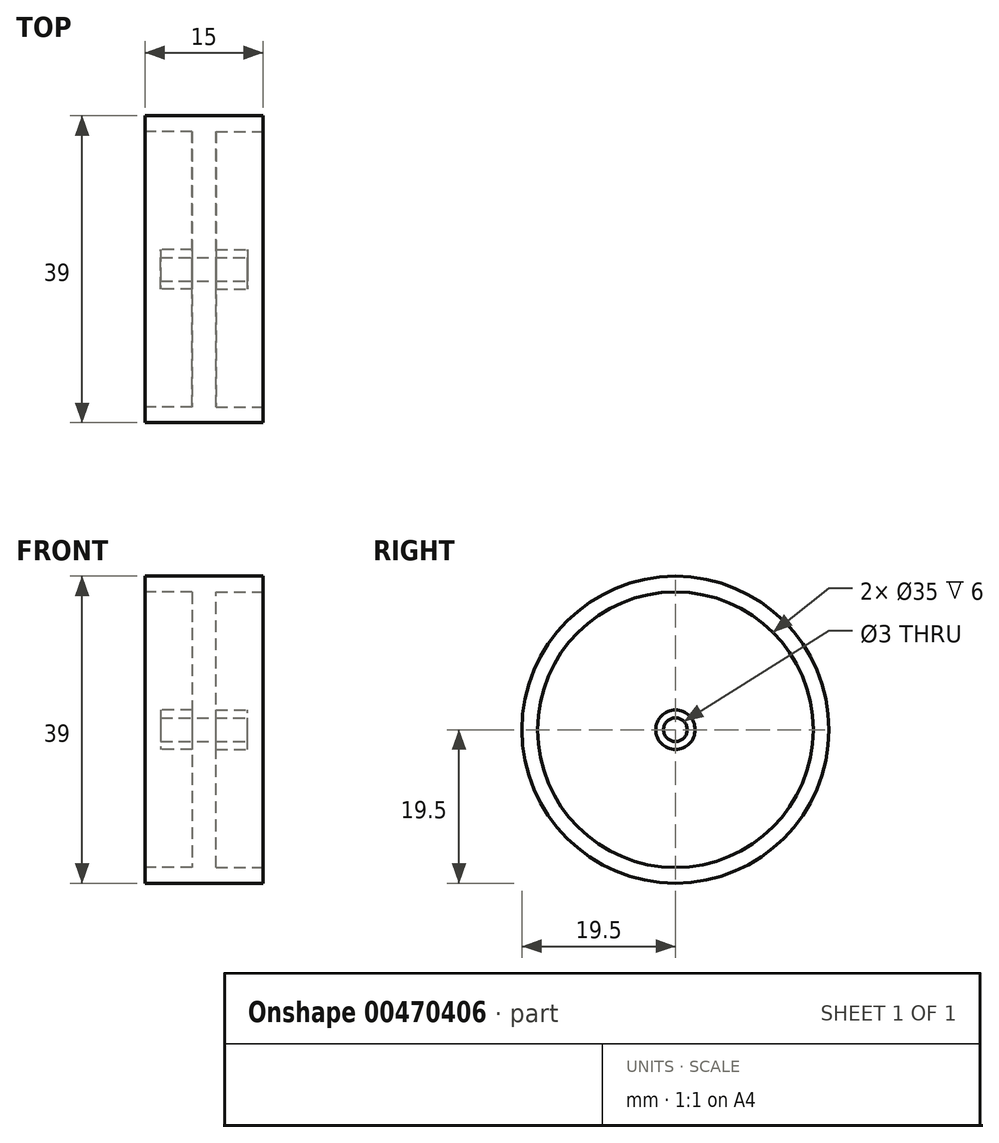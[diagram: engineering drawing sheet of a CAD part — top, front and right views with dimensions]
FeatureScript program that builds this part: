
annotation { "Feature Type Name" : "Feature", "Feature Type Description" : "" }
export const myFeature = defineFeature(function(context is Context, id is Id, definition is map)
    precondition{}
    {
        {
            var Q0;
            Q0=qCreatedBy(makeId("Right.planeOp"),FACE);
            var sketch = newSketch(context, id + "F0", { "sketchPlane" : qUnion([Q0])});
            skCircle(sketch, "E0", {"center": v(0, 0) * mm, "radius": 19.5 * mm});
            skSolve(sketch);
        }
        {
            var Q0;
            Q0=makeQuery(id+"F0.imprint","IMPRINT",FACE,{"disambiguationData":[TD([[makeQuery(id+"F0.imprint","IMPRINT",EDGE,{"derivedFrom":sQuery(id+"F0.wireOp",EDGE,"E0")}),1.0]])]});
            extrude(context, id + "F1", {"entities" : qUnion([Q0]), "endBound" : BoundingType.SYMMETRIC, "depth" : 15 * mm});
        }
        {
            var Q0;
            Q0=makeQuery(id+"F1.opExtrude","CAP_FACE",FACE,{"disambiguationData":[OSD([sQuery(id+"F0.wireOp",EDGE,"E0")])],"isStart":false});
            var sketch = newSketch(context, id + "F2", { "sketchPlane" : qUnion([Q0])});
            skCircle(sketch, "E1", {"center": v(0, 0) * mm, "radius": 17.5 * mm});
            skSolve(sketch);
        }
        {
            var Q0;
            Q0=makeQuery(id+"F1.opExtrude","CAP_FACE",FACE,{"disambiguationData":[OSD([sQuery(id+"F0.wireOp",EDGE,"E0")])],"isStart":true});
            var sketch = newSketch(context, id + "F3", { "sketchPlane" : qUnion([Q0])});
            skCircle(sketch, "E2", {"center": v(0, 0) * mm, "radius": 17.5 * mm});
            skSolve(sketch);
        }
        {
            var Q0;
            Q0=makeQuery(id+"F3.imprint","IMPRINT",FACE,{"disambiguationData":[TD([[makeQuery(id+"F3.imprint","IMPRINT",EDGE,{"derivedFrom":sQuery(id+"F3.wireOp",EDGE,"E2")}),1.0]])]});
            extrude(context, id + "F4", {"entities" : qUnion([Q0]), "operationType" : NewBodyOperationType.REMOVE, "oppositeDirection" : true, "depth" : 2 * mm});
        }
        {
            var Q0;
            Q0=makeQuery(id+"F2.imprint","IMPRINT",FACE,{"disambiguationData":[TD([[makeQuery(id+"F2.imprint","IMPRINT",EDGE,{"derivedFrom":sQuery(id+"F2.wireOp",EDGE,"E1")}),1.0]])]});
            extrude(context, id + "F5", {"entities" : qUnion([Q0]), "operationType" : NewBodyOperationType.REMOVE, "oppositeDirection" : true, "depth" : 2 * mm});
        }
        {
            var Q0;
            Q0=makeQuery(id+"F5.boolean.opBoolean","COPY",FACE,{"derivedFrom":makeQuery(id+"F5.opExtrude","CAP_FACE",FACE,{"disambiguationData":[OSD([sQuery(id+"F2.wireOp",EDGE,"E1")])],"isStart":false})});
            var sketch = newSketch(context, id + "F6", { "sketchPlane" : qUnion([Q0])});
            skCircle(sketch, "E3", {"center": v(0, 0) * mm, "radius": 1.5 * mm});
            skSolve(sketch);
        }
        {
            var Q0;
            Q0=makeQuery(id+"F6.imprint","IMPRINT",FACE,{"disambiguationData":[TD([[makeQuery(id+"F6.imprint","IMPRINT",EDGE,{"derivedFrom":sQuery(id+"F6.wireOp",EDGE,"E3")}),1.0]])]});
            extrude(context, id + "F7", {"entities" : qUnion([Q0]), "operationType" : NewBodyOperationType.REMOVE, "oppositeDirection" : true, "depth" : 25 * mm});
        }
        {
            var Q0;
            Q0=makeQuery(id+"F5.boolean.opBoolean","COPY",FACE,{"derivedFrom":makeQuery(id+"F5.opExtrude","CAP_FACE",FACE,{"disambiguationData":[OSD([sQuery(id+"F2.wireOp",EDGE,"E1")])],"isStart":false})});
            var sketch = newSketch(context, id + "F8", { "sketchPlane" : qUnion([Q0])});
            skCircle(sketch, "E4", {"center": v(0, 0) * mm, "radius": 2.5 * mm});
            skSolve(sketch);
        }
        {
            var Q0;
            Q0=makeQuery(id+"F8.imprint","IMPRINT",FACE,{"disambiguationData":[TD([[makeQuery(id+"F8.imprint","IMPRINT",EDGE,{"derivedFrom":sQuery(id+"F8.wireOp",EDGE,"E4")}),-1.0]])]});
            extrude(context, id + "F9", {"entities" : qUnion([Q0]), "operationType" : NewBodyOperationType.REMOVE, "oppositeDirection" : true, "depth" : 4 * mm});
        }
        {
            var Q0;
            Q0=makeQuery(id+"F4.boolean.opBoolean","COPY",FACE,{"derivedFrom":makeQuery(id+"F4.opExtrude","CAP_FACE",FACE,{"disambiguationData":[OSD([sQuery(id+"F3.wireOp",EDGE,"E2")])],"isStart":false})});
            var sketch = newSketch(context, id + "F10", { "sketchPlane" : qUnion([Q0])});
            skCircle(sketch, "E5", {"center": v(0, 0) * mm, "radius": 2.5 * mm});
            skSolve(sketch);
        }
        {
            var Q0;
            Q0=makeQuery(id+"F10.imprint","IMPRINT",FACE,{"disambiguationData":[TD([[makeQuery(id+"F10.imprint","IMPRINT",EDGE,{"derivedFrom":sQuery(id+"F10.wireOp",EDGE,"E5")}),-1.0]])]});
            extrude(context, id + "F11", {"entities" : qUnion([Q0]), "operationType" : NewBodyOperationType.REMOVE, "oppositeDirection" : true, "depth" : 4 * mm});
        }
    });
